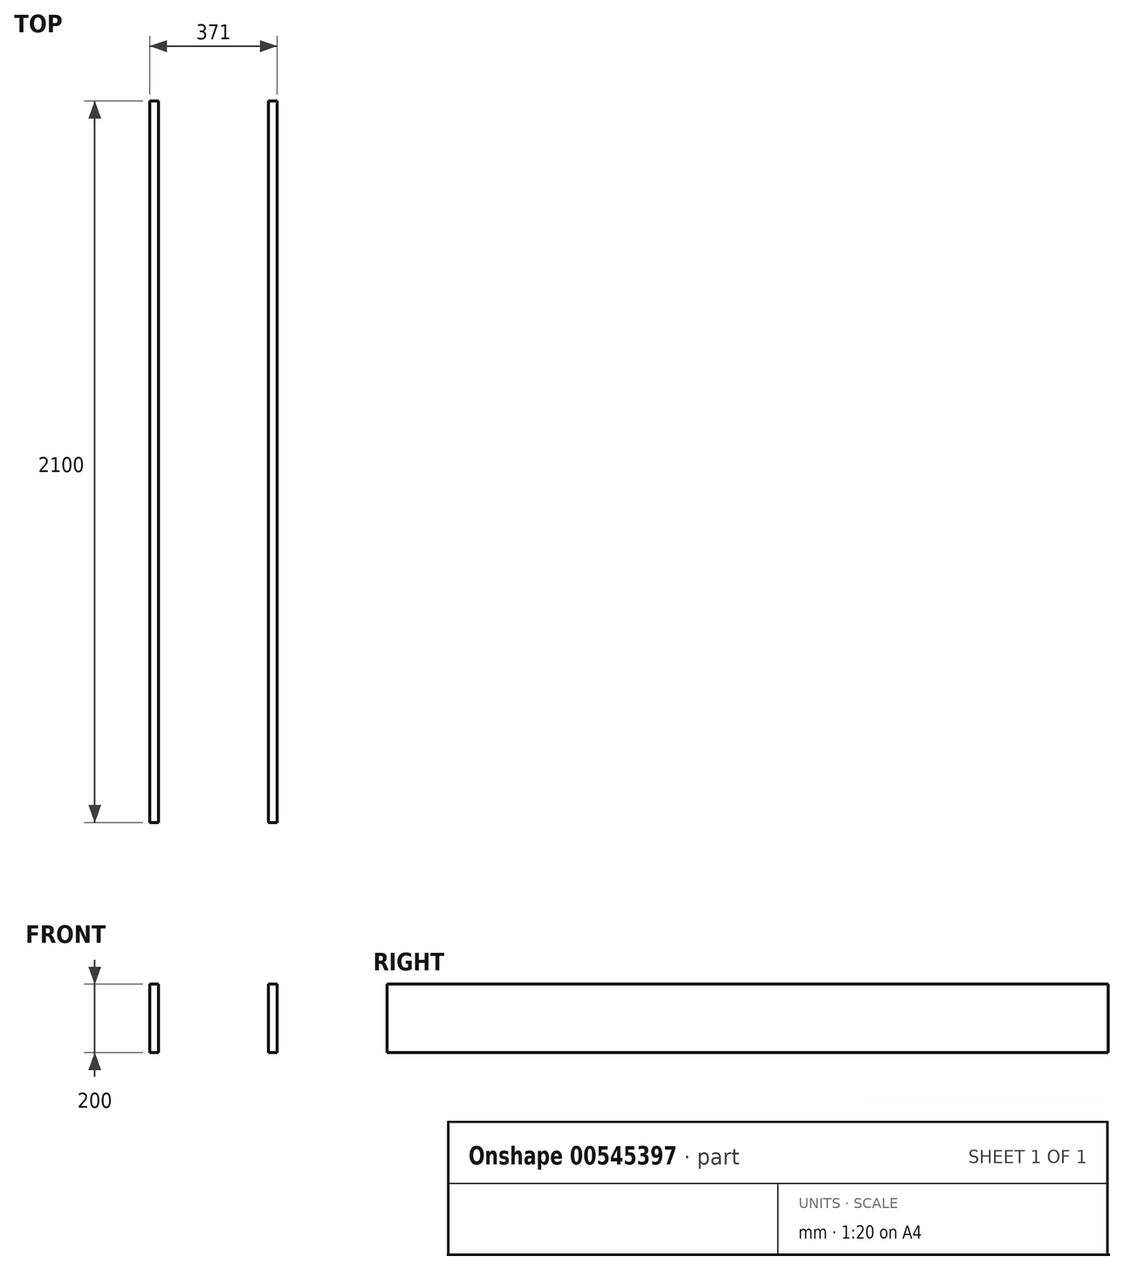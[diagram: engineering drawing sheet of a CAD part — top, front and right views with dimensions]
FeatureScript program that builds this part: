
annotation { "Feature Type Name" : "Feature", "Feature Type Description" : "" }
export const myFeature = defineFeature(function(context is Context, id is Id, definition is map)
    precondition{}
    {
        {
            var Q0;
            Q0=qCreatedBy(makeId("Top.planeOp"),FACE);
            var sketch = newSketch(context, id + "F0", { "sketchPlane" : qUnion([Q0])});
            skLineSegment(sketch, "E0.bottom", {"start": v(0, 0) * mm, "end": v(25, 0) * mm});
            skLineSegment(sketch, "E0.top", {"start": v(0, 2100) * mm, "end": v(25, 2100) * mm});
            skLineSegment(sketch, "E0.left", {"start": v(0, 0) * mm, "end": v(0, 2100) * mm});
            skLineSegment(sketch, "E0.right", {"start": v(25, 0) * mm, "end": v(25, 2100) * mm});
            skSolve(sketch);
        }
        {
            var Q0;
            Q0 = qSketchRegion(id + "F0", true);
            extrude(context, id + "F1", {"entities" : qUnion([Q0]), "depth" : 200 * mm, "offsetDistance" : 25 * mm});
        }
        {
            var Q0;
            Q0=makeQuery(id+"F1.opExtrude","SWEPT_BODY",BODY,{"disambiguationData":[OSD([sQuery(id+"F0.wireOp",EDGE,"E0.bottom"),sQuery(id+"F0.wireOp",EDGE,"E0.top"),sQuery(id+"F0.wireOp",EDGE,"E0.left"),sQuery(id+"F0.wireOp",EDGE,"E0.right")])]});
            transform(context, id + "F2", {"entities" : qUnion([Q0]), "transformType" : TransformType.TRANSLATION_3D, "dx" : 346 * mm, "dy" : 0 * mm, "dz" : 0 * mm, "makeCopy" : true});
        }
    });
